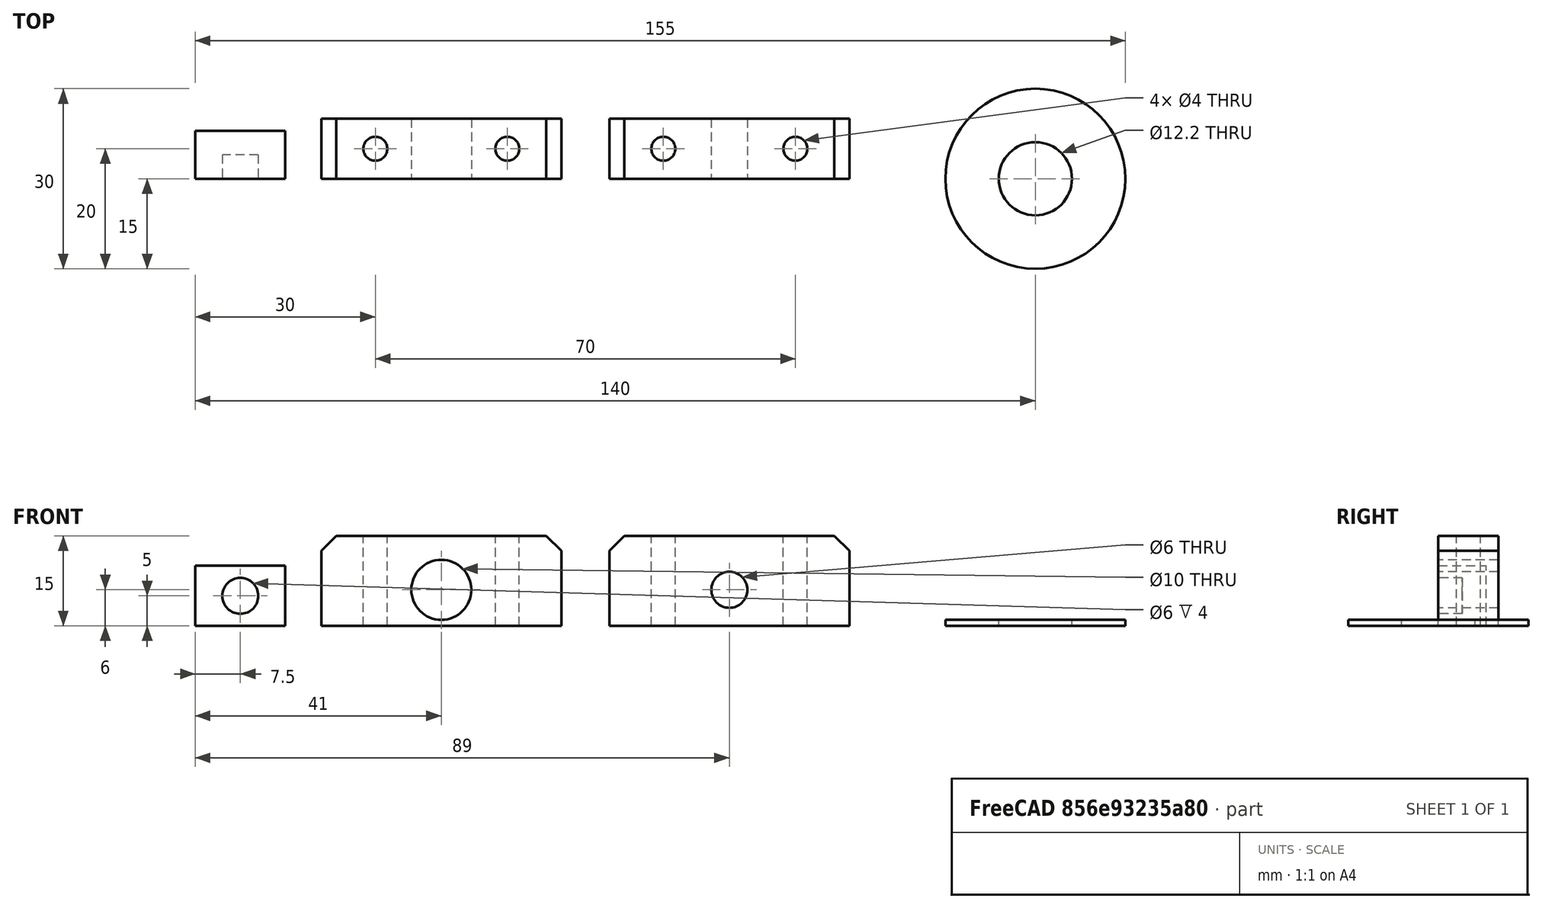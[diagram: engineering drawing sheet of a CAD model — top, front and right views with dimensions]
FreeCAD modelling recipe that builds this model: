
FCSTD DOCUMENT  (FreeCAD 0.15R4671 (Git))
Label: soporte eje hombro dimer
License: All rights reserved
LicenseURL: http://en.wikipedia.org/wiki/All_rights_reserved
objects: Part::Cylinder×9, Part::Cut×6, Part::Box×3, Part::MultiFuse×2, Part::Chamfer×2
note: 22 computed .brp shape members not serialized (recipe doc carries the construction recipe); baked Part::Feature solids carry a one-line shape summary decoded from their .brp

FEATURE [Part::Box] Box  label="Cube"
  Height = 15
  Length = 40
  Width = 10
FEATURE [Part::Cylinder] Cylinder
  Angle = 360
  Height = 13
  Placement = pos=(20,11,6) rot=(1,0,0;1.5708rad)
  Radius = 5
FEATURE [Part::Cut] Cut
  Base = -> Box
  Tool = -> Cylinder
FEATURE [Part::Cylinder] Cylinder001
  Angle = 360
  Height = 22
  Placement = pos=(9,5,0) rot=(0,0,1;0rad)
  Radius = 2
FEATURE [Part::Cylinder] Cylinder002
  Angle = 360
  Height = 22
  Placement = pos=(31,5,0) rot=(0,0,1;0rad)
  Radius = 2
FEATURE [Part::MultiFuse] Fusion
  Shapes = -> [Cylinder002,Cylinder001]
FEATURE [Part::Cut] Cut001
  Base = -> Cut
  Tool = -> Fusion
FEATURE [Part::Chamfer] Chamfer
  Base = -> Cut001
  Edges = 2 edges r=2.5: [Edge2,Edge10]
  Placement = pos=(21,0,0) rot=(0,0,1;0rad)
FEATURE [Part::Box] Box001  label="Cube001"
  Height = 15
  Length = 40
  Width = 10
FEATURE [Part::Cylinder] Cylinder003
  Angle = 360
  Height = 13
  Placement = pos=(20,11,6) rot=(1,0,0;1.5708rad)
  Radius = 3
FEATURE [Part::Cut] Cut002
  Base = -> Box001
  Tool = -> Cylinder003
FEATURE [Part::Cylinder] Cylinder004
  Angle = 360
  Height = 22
  Placement = pos=(9,5,0) rot=(0,0,1;0rad)
  Radius = 2
FEATURE [Part::Cylinder] Cylinder005
  Angle = 360
  Height = 22
  Placement = pos=(31,5,0) rot=(0,0,1;0rad)
  Radius = 2
FEATURE [Part::MultiFuse] Fusion001
  Shapes = -> [Cylinder005,Cylinder004]
FEATURE [Part::Cut] Cut003
  Base = -> Cut002
  Tool = -> Fusion001
FEATURE [Part::Chamfer] Chamfer001  label="chamfer eje del motor"
  Base = -> Cut003
  Edges = 2 edges r=2.5: [Edge2,Edge10]
  Placement = pos=(69,0,0) rot=(0,0,1;0rad)
FEATURE [Part::Cylinder] Cylinder006
  Angle = 360
  Height = 1
  Placement = pos=(140,0,0) rot=(0,0,1;0rad)
  Radius = 15
FEATURE [Part::Cylinder] Cylinder007
  Angle = 360
  Height = 1
  Placement = pos=(140,0,0) rot=(0,0,1;0rad)
  Radius = 6.1
FEATURE [Part::Cut] Cut004  label="arandela motor"
  Base = -> Cylinder006
  Tool = -> Cylinder007
FEATURE [Part::Box] Box002  label="Cube002"
  Height = 10
  Length = 15
  Placement = pos=(0,-50,0) rot=(0,0,1;0rad)
  Width = 8
FEATURE [Part::Cylinder] Cylinder008
  Angle = 360
  Height = 10
  Placement = pos=(7.5,-46,5) rot=(1,0,0;1.5708rad)
  Radius = 3
FEATURE [Part::Cut] Cut005  label="amarre barra motor"
  Base = -> Box002
  Placement = pos=(0,50,0) rot=(0,0,1;0rad)
  Tool = -> Cylinder008
